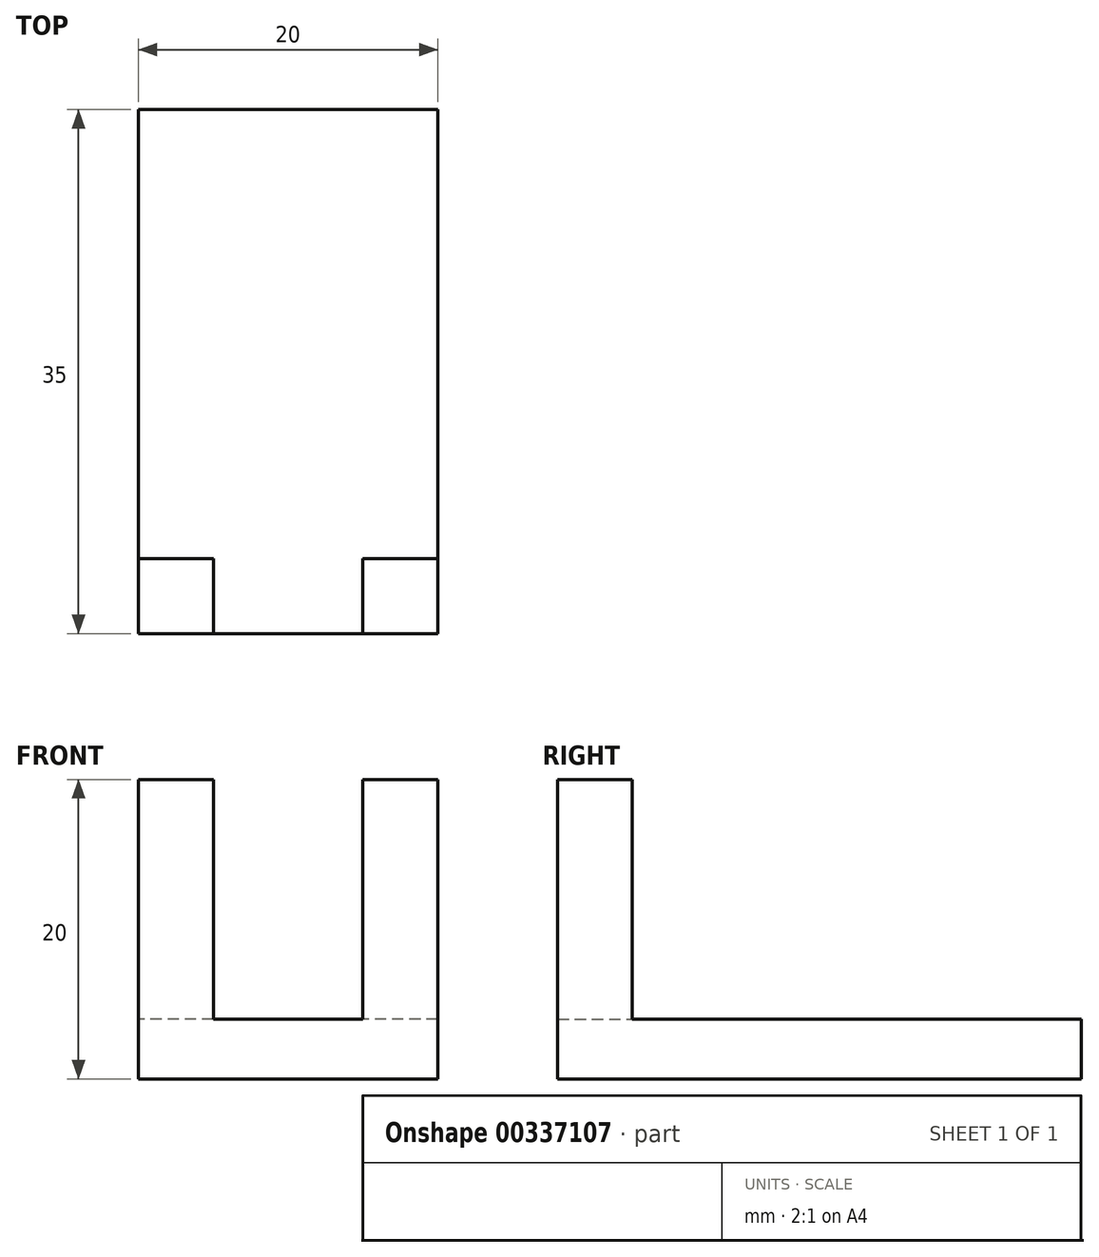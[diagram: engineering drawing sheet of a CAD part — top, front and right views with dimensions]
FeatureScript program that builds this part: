
annotation { "Feature Type Name" : "Feature", "Feature Type Description" : "" }
export const myFeature = defineFeature(function(context is Context, id is Id, definition is map)
    precondition{}
    {
        {
            var Q0;
            Q0=qCreatedBy(makeId("Top.planeOp"),FACE);
            var sketch = newSketch(context, id + "F0", { "sketchPlane" : qUnion([Q0])});
            skLineSegment(sketch, "E0.bottom", {"start": v(-44.5, 40.24) * mm, "end": v(-24.5, 40.24) * mm});
            skLineSegment(sketch, "E0.top", {"start": v(-44.5, 5.24) * mm, "end": v(-24.5, 5.24) * mm});
            skLineSegment(sketch, "E0.left", {"start": v(-44.5, 40.24) * mm, "end": v(-44.5, 5.24) * mm});
            skLineSegment(sketch, "E0.right", {"start": v(-24.5, 40.24) * mm, "end": v(-24.5, 5.24) * mm});
            skLineSegment(sketch, "E1", {"start": v(-44.5, 40.24) * mm, "end": v(-39.5, 40.24) * mm});
            skLineSegment(sketch, "E2", {"start": v(-39.5, 40.24) * mm, "end": v(-39.5, 35.26) * mm});
            skLineSegment(sketch, "E3", {"start": v(-39.5, 35.26) * mm, "end": v(-44.5, 35.26) * mm});
            skLineSegment(sketch, "E4", {"start": v(-24.5, 40.24) * mm, "end": v(-29.5, 40.24) * mm});
            skLineSegment(sketch, "E5", {"start": v(-29.5, 40.24) * mm, "end": v(-29.5, 35.26) * mm});
            skLineSegment(sketch, "E6", {"start": v(-29.5, 35.26) * mm, "end": v(-24.5, 35.26) * mm});
            skLineSegment(sketch, "E7", {"start": v(-29.5, 5.24) * mm, "end": v(-29.5, 10.24) * mm});
            skLineSegment(sketch, "E8", {"start": v(-29.5, 10.24) * mm, "end": v(-24.5, 10.24) * mm});
            skLineSegment(sketch, "E9", {"start": v(-44.5, 10.24) * mm, "end": v(-39.5, 10.24) * mm});
            skLineSegment(sketch, "E10", {"start": v(-39.5, 10.24) * mm, "end": v(-39.5, 5.24) * mm});
            skSolve(sketch);
        }
        {
            var Q0;
            Q0=qSketchRegion(id+"F0",true);
            extrude(context, id + "F1", {"entities" : qUnion([Q0]), "depth" : 4 * mm, "offsetDistance" : 25 * mm});
        }
        {
            var Q0;
            {var subQ0=sQuery(id+"F0.wireOp",EDGE,"E4");Q0=makeQuery(id+"F0.imprint","IMPRINT",FACE,{"disambiguationData":[TD([[makeQuery(id+"F0.imprint","IMPRINT",EDGE,{"derivedFrom":subQ0}),1.0]])]});}
            var Q1;
            {var subQ0=sQuery(id+"F0.wireOp",EDGE,"E1");Q1=makeQuery(id+"F0.imprint","IMPRINT",FACE,{"disambiguationData":[TD([[makeQuery(id+"F0.imprint","IMPRINT",EDGE,{"derivedFrom":subQ0}),-1.0]])]});}
            var Q2;
            {var subQ4=sQuery(id+"F0.wireOp",EDGE,"E9");Q2=makeQuery(id+"F0.imprint","IMPRINT",FACE,{"disambiguationData":[TD([[makeQuery(id+"F0.imprint","IMPRINT",EDGE,{"derivedFrom":subQ4}),-1.0]])]});}
            var Q3;
            {var subQ3=sQuery(id+"F0.wireOp",EDGE,"E7");Q3=makeQuery(id+"F0.imprint","IMPRINT",FACE,{"disambiguationData":[TD([[makeQuery(id+"F0.imprint","IMPRINT",EDGE,{"derivedFrom":subQ3}),-1.0]])]});}
            extrude(context, id + "F2", {"entities" : qUnion([Q0, Q1, Q2, Q3]), "operationType" : NewBodyOperationType.ADD, "depth" : 20 * mm, "offsetDistance" : 25 * mm});
        }
    });
